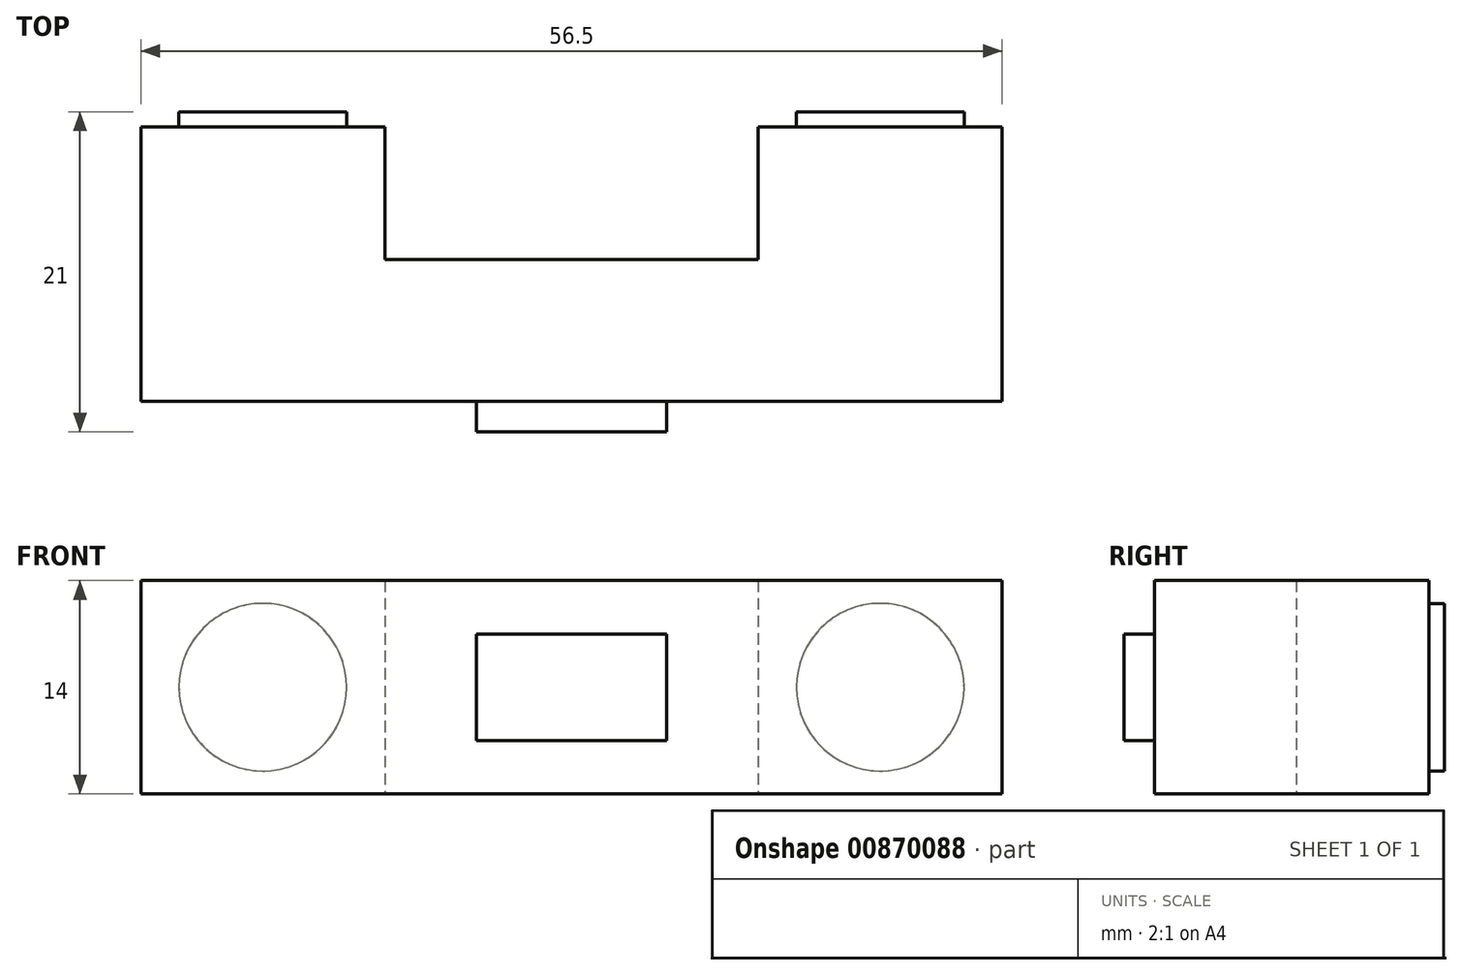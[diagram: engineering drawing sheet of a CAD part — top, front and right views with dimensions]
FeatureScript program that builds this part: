
annotation { "Feature Type Name" : "Feature", "Feature Type Description" : "" }
export const myFeature = defineFeature(function(context is Context, id is Id, definition is map)
    precondition{}
    {
        {
            var Q0;
            Q0=qCreatedBy(makeId("Top.planeOp"),FACE);
            var sketch = newSketch(context, id + "F0", { "sketchPlane" : qUnion([Q0])});
            skLineSegment(sketch, "E0.bottom", {"start": v(28.25, 9) * mm, "end": v(-28.25, 9) * mm});
            skLineSegment(sketch, "E0.top", {"start": v(28.25, -9) * mm, "end": v(-28.25, -9) * mm});
            skLineSegment(sketch, "E0.left", {"start": v(28.25, 9) * mm, "end": v(28.25, -9) * mm});
            skLineSegment(sketch, "E0.right", {"start": v(-28.25, 9) * mm, "end": v(-28.25, -9) * mm});
            skPoint(sketch, "E0.middle", {"position": v(0, 0) * mm});
            skLineSegment(sketch, "E1", {"start": v(28.25, 9) * mm, "end": v(12.25, 9) * mm});
            skLineSegment(sketch, "E2", {"start": v(-28.25, 9) * mm, "end": v(-12.25, 9) * mm});
            skLineSegment(sketch, "E3", {"start": v(12.25, -9) * mm, "end": v(12.25, 0.3) * mm});
            skLineSegment(sketch, "E4", {"start": v(12.25, 9) * mm, "end": v(12.25, 0.3) * mm});
            skLineSegment(sketch, "E5", {"start": v(12.25, 0.3) * mm, "end": v(-12.25, 0.3) * mm});
            skLineSegment(sketch, "E6", {"start": v(-12.25, 0.3) * mm, "end": v(-12.25, 9) * mm});
            skSolve(sketch);
        }
        {
            var Q0;
            {var subQ2=sQuery(id+"F0.wireOp",EDGE,"E0.right");Q0=makeQuery(id+"F0.imprint","IMPRINT",FACE,{"disambiguationData":[TD([[makeQuery(id+"F0.imprint","IMPRINT",EDGE,{"derivedFrom":subQ2}),1.0]])]});}
            var Q1;
            {var subQ0=sQuery(id+"F0.wireOp",EDGE,"E0.left");Q1=makeQuery(id+"F0.imprint","IMPRINT",FACE,{"disambiguationData":[TD([[makeQuery(id+"F0.imprint","IMPRINT",EDGE,{"derivedFrom":subQ0}),-1.0]])]});}
            extrude(context, id + "F1", {"entities" : qUnion([Q0, Q1]), "depth" : 14 * mm, "offsetDistance" : 25 * mm});
        }
        {
            var Q0;
            {var subQ0=sQuery(id+"F0.wireOp",EDGE,"E0.bottom");Q0=makeQuery(id+"F1.opExtrude","SWEPT_FACE",FACE,{"disambiguationData":[OSD([subQ0]),TDD([makeQuery(id+"F0.imprint","IMPRINT",EDGE,{"disambiguationData":[TD([[makeQuery(id+"F0.imprint","INTERSECT",VERTEX,{"derivedFrom":[subQ0,sQuery(id+"F0.wireOp",EDGE,"E0.right")]}),1.0]])],"derivedFrom":subQ0})])]});}
            var sketch = newSketch(context, id + "F2", { "sketchPlane" : qUnion([Q0])});
            skCircle(sketch, "E7", {"center": v(-20.25, 7) * mm, "radius": 5.5 * mm});
            skPoint(sketch, "E7.centerSnap0", {"position": v(-12.25, 7) * mm});
            skPoint(sketch, "E7.centerSnap1", {"position": v(-20.25, 14) * mm});
            skCircle(sketch, "E8", {"center": v(20.25, 7) * mm, "radius": 5.5 * mm});
            skPoint(sketch, "E8.centerSnap0", {"position": v(20.25, 14) * mm});
            skPoint(sketch, "E8.centerSnap1", {"position": v(12.25, 7) * mm});
            skSolve(sketch);
        }
        {
            var Q0;
            Q0=makeQuery(id+"F2.imprint","IMPRINT",FACE,{"disambiguationData":[TD([[makeQuery(id+"F2.imprint","IMPRINT",EDGE,{"derivedFrom":sQuery(id+"F2.wireOp",EDGE,"E7")}),1.0]])]});
            var Q1;
            Q1=makeQuery(id+"F2.imprint","IMPRINT",FACE,{"disambiguationData":[TD([[makeQuery(id+"F2.imprint","IMPRINT",EDGE,{"derivedFrom":sQuery(id+"F2.wireOp",EDGE,"E8")}),1.0]])]});
            extrude(context, id + "F3", {"entities" : qUnion([Q0, Q1]), "operationType" : NewBodyOperationType.ADD, "depth" : 1 * mm, "offsetDistance" : 25 * mm});
        }
        {
            var Q0;
            Q0=makeQuery(id+"F1.opExtrude","SWEPT_FACE",FACE,{"disambiguationData":[OSD([sQuery(id+"F0.wireOp",EDGE,"E0.top")])]});
            var sketch = newSketch(context, id + "F4", { "sketchPlane" : qUnion([Q0])});
            skLineSegment(sketch, "E9", {"start": v(0, 0) * mm, "end": v(0, 3.5) * mm});
            skLineSegment(sketch, "E10", {"start": v(0, 14) * mm, "end": v(0, 10.5) * mm});
            skLineSegment(sketch, "E11", {"start": v(0, 3.5) * mm, "end": v(0, 7.5) * mm});
            skLineSegment(sketch, "E12.bottom", {"start": v(6.25, 3.5) * mm, "end": v(-6.25, 3.5) * mm});
            skLineSegment(sketch, "E12.top", {"start": v(6.25, 10.5) * mm, "end": v(-6.25, 10.5) * mm});
            skLineSegment(sketch, "E12.left", {"start": v(6.25, 3.5) * mm, "end": v(6.25, 10.5) * mm});
            skLineSegment(sketch, "E12.right", {"start": v(-6.25, 3.5) * mm, "end": v(-6.25, 10.5) * mm});
            skPoint(sketch, "E12.middle", {"position": v(0, 7.5) * mm});
            skSolve(sketch);
        }
        {
            var Q0;
            {var subQ3=sQuery(id+"F4.wireOp",EDGE,"E12.left");Q0=makeQuery(id+"F4.imprint","IMPRINT",FACE,{"disambiguationData":[TD([[makeQuery(id+"F4.imprint","IMPRINT",EDGE,{"derivedFrom":subQ3}),1.0]])]});}
            extrude(context, id + "F5", {"entities" : qUnion([Q0]), "operationType" : NewBodyOperationType.ADD, "depth" : 2 * mm, "offsetDistance" : 25 * mm});
        }
    });
